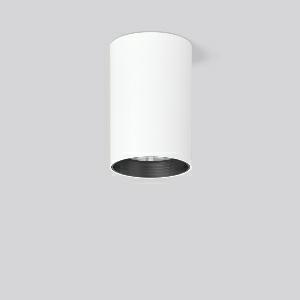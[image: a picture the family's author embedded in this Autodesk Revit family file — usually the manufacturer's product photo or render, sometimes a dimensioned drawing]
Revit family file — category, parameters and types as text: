
# Revit family: heledon_maxi_a_931229_002_1_cc65
name_source: partatom
category: Lighting Fixtures
units: mm (PartAtom-declared; Revit-internal decimal feet)

## family parameters
Cut with Voids When Loaded = No
Host = Face
Light Source = No
Part Type = Normal
Room Calculation Point = No
Round Connector Dimension = Use Diameter
Shared = No

## types (1)
- HELEDON maxi A (1 x LED Modul 940, 3800 lm, 4000)
    Apparent Load = 35 VA
    Approval mark = CE
    CIE Flux Codes = 96 100 100 100 100
    Color Rendering = 92
    Color Temperature = 4000
    Default Elevation = 1800 mm
    Description = Series: HELEDON maxi
Cylindrical surface-mounted downlight. Housing: die-cast aluminium, powder-coated. Internal ceiling frame polycarbonate with bayonet mounting. Black plastic ring and recessed LED to prevent glare from the side. Optical assembly with lens made of plastic (polycarbonate) for the best homogeneous light distribution - can be changed without tools. Best colour rendering index Ra>90. Suitable for Ceiling mounting. Easy installation with a separate ceiling frame with bayonet mounting and plug connection. Driver integrated. Connected via plug-in connector. High quality converter without flickering and stroboscopic effect. The following accessories can be mounted without use of tools: interchangeable lenses, decorative glasses, honeycomb louvre, clear and frosted diffusers, white interchangeable plastic ring. 
Colour: traffic white, matt (RAL 9016)
Diameter: 123 mm
Height: 183 mm
Lamp: LED
Socket: without socket
Colour temperature: 4000K
Colour rendering index (CRI): 92
System power: 35 W
Rated luminous flux: 3800 lm
Luminous efficiency: 109 lm/W
Control gear: Regulated power supply
Protection class: I
Type of protection: IP 20
    Height = 183 mm
    Lamp = 1 x LED Modul 940
    Lamp Light Flux = 3800 lm
    Lamp count = 1
    Length = 123 mm
    Lifetime = 50000 h
    Luminous efficacy = 109 lm/W
    Manufacturer = RZB
    ModVariant = No
    Model = 931229.002.1
    Mounting Place = Ceiling
    Mounting Type = Surface mounted
    Number of Poles = 1
    OnlyDefault = Yes
    Power Factor = 1
    Product Name = HELEDON maxi A
    Product group = Surface mounted downlights
    ProductGroupID = 302
    Protection Class = Protection class I
    Protection Degree = IP 20
    RLX_Detail_Level = 1
    RLX_Emergency_Light_Flux = 0 lm
    RLX_Emergency_Type = 0
    RLX_Emergency_Type_DB = No
    RlxData = <blob elided: 96093 chars, md5=3f9c1ed1>
    Socket = socket
    Standby Power = 0 W
    System Light Flux = 3800 lm
    System Power = 35 W
    Type Comments = Product without accessories
    Type Image = 931193.002.jpg
    URL = http://relux.com
    VarID = ---
    Voltage = 230 V
    Voltage Range = 220-240 V
    Weight = 0.00 kg
    Width = 0 mm  [stored 0 ft]

note: [stored X ft] marks values corroborated as IEEE doubles in the binary element streams (Revit-internal decimal feet)

## geometry (parser evidence)
native form markers: Blend x4, Sweep x10
no freeform markers — native parametric forms only
